# Revit family: RPFI_FSN2E_1.0_to_2.5_LOD_400
name_source: partatom
category: Equipement de génie climatique
revit_build: Autodesk Revit 2016 (Build: 20150220_1215(x64)
units: mm (PartAtom-declared; Revit-internal decimal feet)

## family parameters
Basée sur le plan de construction = Non
Cote de connecteur circulaire = Utiliser le diamètre
Couper avec des vides une fois chargée = Non
Numéro OmniClass = 23.75.00.00
Partagée = Non
Point de calcul de pièce = Non
Titre OmniClass = Climate Control (HVAC)
Toujours verticalement = Oui
Type d'élément = Normal

## types (4) — shared parameters
Air outlet = 20 mm  [stored 0.0656168 ft]
BC_OBJECT_ID = 6678
Color = Spring white (4.1Y8.5/0.7)
Commentaires du type = RPFI FSN2E
Diamètre Eau Sortie = 19 mm
Electrical box (high) distance = 30 mm  [stored 0.0984252 ft]
Electrical box (low) distance = 30 mm  [stored 0.0984252 ft]
Fabricant = HITACHI
Frequency = 50 Hz
Input Height = 50 mm  [stored 0.164042 ft]
Maximum AC Voltage = 253 V
Minimum AC Voltage = 207 V
Nominal Voltage = 230 V
Number of Poles = 1
Output Width = 122 mm
Overall Depth = 220 mm
Overall Height = 600 mm
Refrigerant = R410A (factory-charged corrosion-proof nitrogen)
Sound power level dB(A) = 60
Usage Current = 5 A

## per-type parameters (varying)
| type | Air flow Speed (high/medium/low) m3/min | Air inlet | Cooling Capacity | Diamètre Eau Entrée | Diamètre Gaz Entrée | Fan motor type (output) | Heating Capacity | Mass | Maximum Air Flow | Minimum Air Flow | Output Height | Overall Width | Sound power at medium load (dB(A)) | Sound power at minimal load (dB(A)) | Sound power max (dB(A)) | Sound pressure level (High/med/low) dB (A) |
| RPFI FSN2E 1.0 | 16/14/11 | 704 mm  [stored 2.30971 ft] | 5 kW | 6 mm  [stored 0.019685 ft] | 18 mm  [stored 0.0590551 ft] | 45 W | 6 kW | 27.00 kg | 16000.0 L/min | 11000.0 L/min | 704 mm  [stored 2.30971 ft] | 754 mm | 36 | 32 | 39 | 39/36/32 |
| RPFI FSN2E 1.5 | 12/10/9 | 829 mm | 4 kW | 6 mm  [stored 0.019685 ft] | 15 mm | 28 W | 4 kW | 23.00 kg | 12000.0 L/min | 9000.0 L/min | 829 mm | 879 mm | 35 | 31 | 38 | 38/35/31 |
| RPFI FSN2E 2.5 | 16/14/11 | 1079 mm | 6 kW | 10 mm  [stored 0.0328084 ft] | 18 mm  [stored 0.0590551 ft] | 45 W | 6 kW | 28.00 kg | 16000.0 L/min | 11000.0 L/min | 1079 mm | 1129 mm | 38 | 34 | 42 | 42/38/34 |
| RPFI FSN2E 2.0 | 16/14/11 | 1079 mm | 5 kW | 6 mm  [stored 0.019685 ft] | 18 mm  [stored 0.0590551 ft] | 45 W | 6 kW | 27.00 kg | 16000.0 L/min | 11000.0 L/min | 1079 mm | 1129 mm | 36 | 32 | 39 | 39/36/32 |

note: [stored X ft] marks values corroborated as IEEE doubles in the binary element streams (Revit-internal decimal feet)

## geometry (parser evidence)
native form markers: Blend x2
no freeform markers — native parametric forms only
